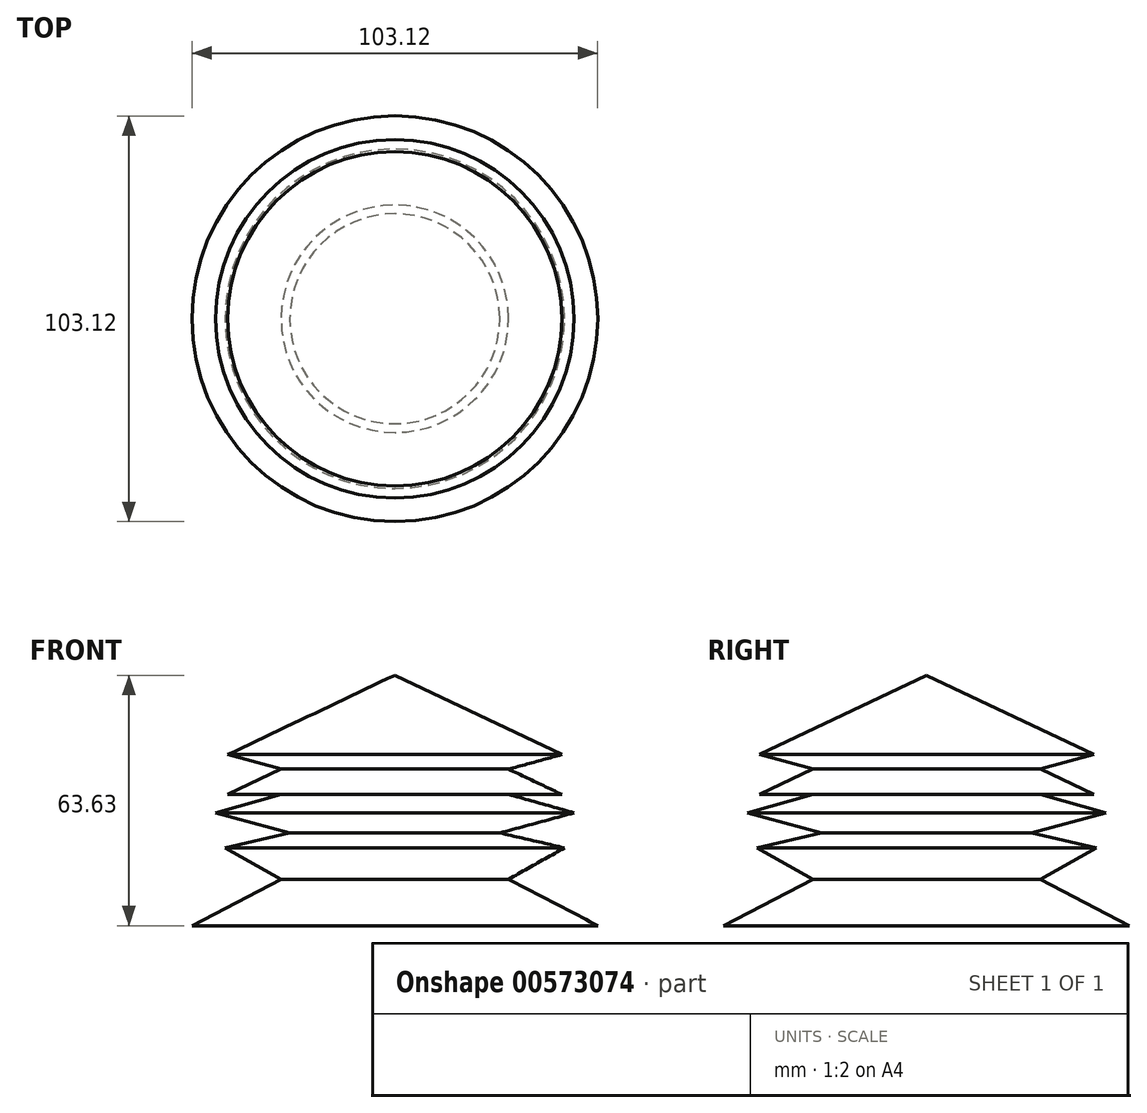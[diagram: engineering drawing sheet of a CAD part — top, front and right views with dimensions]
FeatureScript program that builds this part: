
annotation { "Feature Type Name" : "Feature", "Feature Type Description" : "" }
export const myFeature = defineFeature(function(context is Context, id is Id, definition is map)
    precondition{}
    {
        {
            var Q0;
            Q0=qCreatedBy(makeId("Front.planeOp"),FACE);
            var sketch = newSketch(context, id + "F0", { "sketchPlane" : qUnion([Q0])});
            skLineSegment(sketch, "E0", {"start": v(0, 0) * mm, "end": v(-51.56, 0) * mm});
            skLineSegment(sketch, "E1", {"start": v(-51.56, 0) * mm, "end": v(-28.9, 11.78) * mm});
            skLineSegment(sketch, "E2", {"start": v(-28.9, 11.78) * mm, "end": v(-43.12, 19.78) * mm});
            skLineSegment(sketch, "E3", {"start": v(-43.12, 19.78) * mm, "end": v(-26.67, 23.56) * mm});
            skLineSegment(sketch, "E4", {"start": v(-26.67, 23.56) * mm, "end": v(-45.56, 28.67) * mm});
            skLineSegment(sketch, "E5", {"start": v(-45.56, 28.67) * mm, "end": v(-28.9, 33.34) * mm});
            skLineSegment(sketch, "E6", {"start": v(-28.9, 33.34) * mm, "end": v(-42.45, 33.34) * mm});
            skLineSegment(sketch, "E7", {"start": v(-42.45, 33.34) * mm, "end": v(-28.9, 39.78) * mm});
            skLineSegment(sketch, "E8", {"start": v(-28.9, 39.78) * mm, "end": v(-42.45, 43.45) * mm});
            skLineSegment(sketch, "E9", {"start": v(-42.45, 43.45) * mm, "end": v(0, 63.63) * mm});
            skLineSegment(sketch, "E10", {"start": v(0, 63.63) * mm, "end": v(0, 0) * mm});
            skSolve(sketch);
        }
        {
            var Q0;
            Q0=makeQuery(id+"F0.imprint","IMPRINT",FACE,{"disambiguationData":[TD([[makeQuery(id+"F0.imprint","IMPRINT",EDGE,{"derivedFrom":sQuery(id+"F0.wireOp",EDGE,"E0")}),-1.0]])]});
            var Q1;
            Q1=sQuery(id+"F0.wireOp",EDGE,"E10");
            revolve(context, id + "F1", {"entities" : qUnion([Q0]), "axis" : qUnion([Q1]), "revolveType" : RevolveType.FULL});
        }
    });
